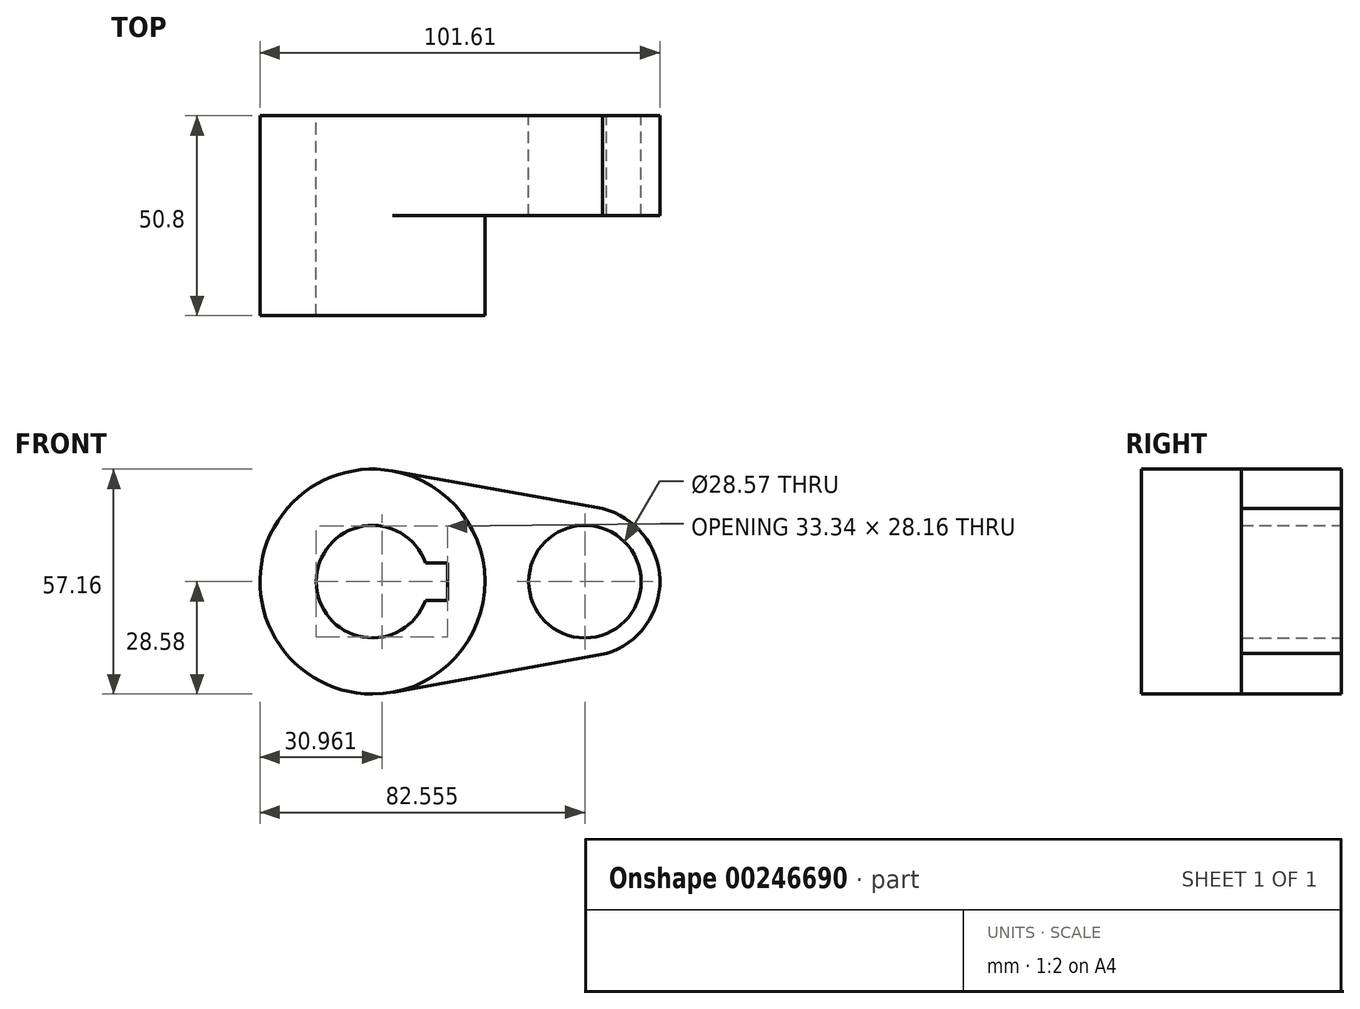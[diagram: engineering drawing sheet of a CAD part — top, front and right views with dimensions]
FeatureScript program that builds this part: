
annotation { "Feature Type Name" : "Feature", "Feature Type Description" : "" }
export const myFeature = defineFeature(function(context is Context, id is Id, definition is map)
    precondition{}
    {
        {
            var Q0;
            Q0=qCreatedBy(makeId("Front.planeOp"),FACE);
            var sketch = newSketch(context, id + "F0", { "sketchPlane" : qUnion([Q0])});
            skCircle(sketch, "E0", {"center": v(0, 0) * mm, "radius": 28.58 * mm});
            skCircle(sketch, "E1", {"center": v(53.98, 0) * mm, "radius": 19.05 * mm});
            skLineSegment(sketch, "E2", {"start": v(5.06, 28.12) * mm, "end": v(58.42, 18.52) * mm});
            skLineSegment(sketch, "E3", {"start": v(5.1, -28.11) * mm, "end": v(59.47, -18.24) * mm});
            skCircle(sketch, "E4", {"center": v(0, 0) * mm, "radius": 14.29 * mm});
            skCircle(sketch, "E5", {"center": v(53.98, 0) * mm, "radius": 14.29 * mm});
            skLineSegment(sketch, "E6.bottom", {"start": v(-19.05, 4.76) * mm, "end": v(19.05, 4.76) * mm});
            skLineSegment(sketch, "E6.top", {"start": v(-19.05, -4.76) * mm, "end": v(19.05, -4.76) * mm});
            skLineSegment(sketch, "E6.left", {"start": v(-19.05, 4.76) * mm, "end": v(-19.05, -4.76) * mm});
            skLineSegment(sketch, "E6.right", {"start": v(19.05, 4.76) * mm, "end": v(19.05, -4.76) * mm});
            skSolve(sketch);
        }
        {
            var Q0;
            {var subQ10=sQuery(id+"F0.wireOp",EDGE,"E6.left");Q0=makeQuery(id+"F0.imprint","IMPRINT",FACE,{"disambiguationData":[TD([[makeQuery(id+"F0.imprint","IMPRINT",EDGE,{"derivedFrom":subQ10}),-1.0]])]});}
            var Q1;
            {var subQ0=sQuery(id+"F0.wireOp",EDGE,"E2");var subQ1=sQuery(id+"F0.wireOp",EDGE,"E0");var subQ2=makeQuery(id+"F0.imprint","INTERSECT",VERTEX,{"derivedFrom":[subQ1,subQ0]});Q1=makeQuery(id+"F0.imprint","IMPRINT",FACE,{"disambiguationData":[TD([[makeQuery(id+"F0.imprint","IMPRINT",EDGE,{"disambiguationData":[TD([[subQ2,1.0]])],"derivedFrom":subQ1}),-1.0]])]});}
            var Q2;
            Q2=makeQuery(id+"F0.imprint","IMPRINT",FACE,{"disambiguationData":[TD([[makeQuery(id+"F0.imprint","IMPRINT",EDGE,{"derivedFrom":sQuery(id+"F0.wireOp",EDGE,"E5")}),-1.0]])]});
            var Q3;
            {var subQ5=sQuery(id+"F0.wireOp",EDGE,"E6.left");Q3=makeQuery(id+"F0.imprint","IMPRINT",FACE,{"disambiguationData":[TD([[makeQuery(id+"F0.imprint","IMPRINT",EDGE,{"derivedFrom":subQ5}),1.0]])]});}
            extrude(context, id + "F1", {"entities" : qUnion([Q0, Q1, Q2, Q3]), "depth" : 25.4 * mm});
        }
        {
            var Q0;
            {var subQ10=sQuery(id+"F0.wireOp",EDGE,"E6.left");Q0=makeQuery(id+"F0.imprint","IMPRINT",FACE,{"disambiguationData":[TD([[makeQuery(id+"F0.imprint","IMPRINT",EDGE,{"derivedFrom":subQ10}),-1.0]])]});}
            var Q1;
            {var subQ5=sQuery(id+"F0.wireOp",EDGE,"E6.left");Q1=makeQuery(id+"F0.imprint","IMPRINT",FACE,{"disambiguationData":[TD([[makeQuery(id+"F0.imprint","IMPRINT",EDGE,{"derivedFrom":subQ5}),1.0]])]});}
            extrude(context, id + "F2", {"entities" : qUnion([Q0, Q1]), "operationType" : NewBodyOperationType.ADD, "depth" : 50.8 * mm});
        }
    });
